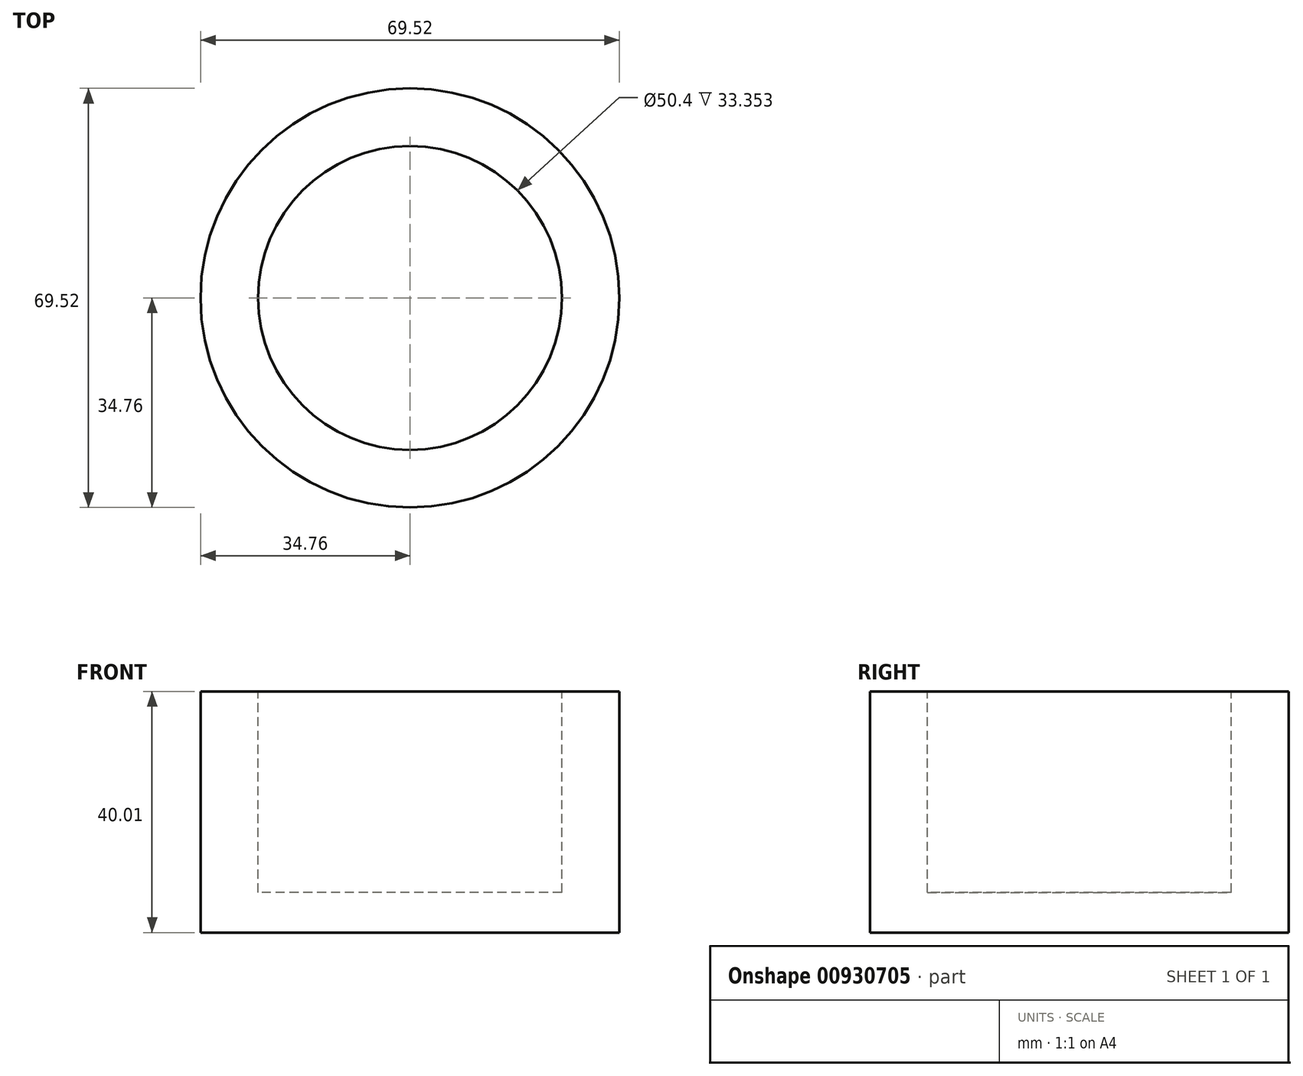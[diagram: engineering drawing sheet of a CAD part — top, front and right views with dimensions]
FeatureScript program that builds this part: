
annotation { "Feature Type Name" : "Feature", "Feature Type Description" : "" }
export const myFeature = defineFeature(function(context is Context, id is Id, definition is map)
    precondition{}
    {
        {
            var Q0;
            Q0=qCreatedBy(makeId("Front.planeOp"),FACE);
            var sketch = newSketch(context, id + "F0", { "sketchPlane" : qUnion([Q0])});
            skLineSegment(sketch, "E0.left", {"start": v(0, 0) * mm, "end": v(0, 0) * mm});
            skLineSegment(sketch, "E1", {"start": v(0, 0) * mm, "end": v(-34.76, 0) * mm});
            skLineSegment(sketch, "E2", {"start": v(-34.76, 0) * mm, "end": v(-34.76, 40) * mm});
            skLineSegment(sketch, "E3", {"start": v(-34.76, 40) * mm, "end": v(-25.2, 40) * mm});
            skLineSegment(sketch, "E4", {"start": v(-25.2, 40) * mm, "end": v(-25.2, 24.64) * mm});
            skLineSegment(sketch, "E5", {"start": v(-25.2, 24.64) * mm, "end": v(-25.2, 6.65) * mm});
            skLineSegment(sketch, "E6", {"start": v(-25.2, 6.65) * mm, "end": v(0, 6.65) * mm});
            skLineSegment(sketch, "E7", {"start": v(0, 6.65) * mm, "end": v(0, 0) * mm});
            skSolve(sketch);
        }
        {
            var Q0;
            Q0=makeQuery(id+"F0.imprint","IMPRINT",FACE,{"disambiguationData":[TD([[makeQuery(id+"F0.imprint","IMPRINT",EDGE,{"derivedFrom":sQuery(id+"F0.wireOp",EDGE,"E1")}),-1.0]])]});
            var Q1;
            Q1=sQuery(id+"F0.wireOp",EDGE,"E7");
            revolve(context, id + "F1", {"surfaceOperationType" : NewSurfaceOperationType.NEW, "entities" : qUnion([Q0]), "axis" : qUnion([Q1]), "revolveType" : RevolveType.FULL});
        }
    });
